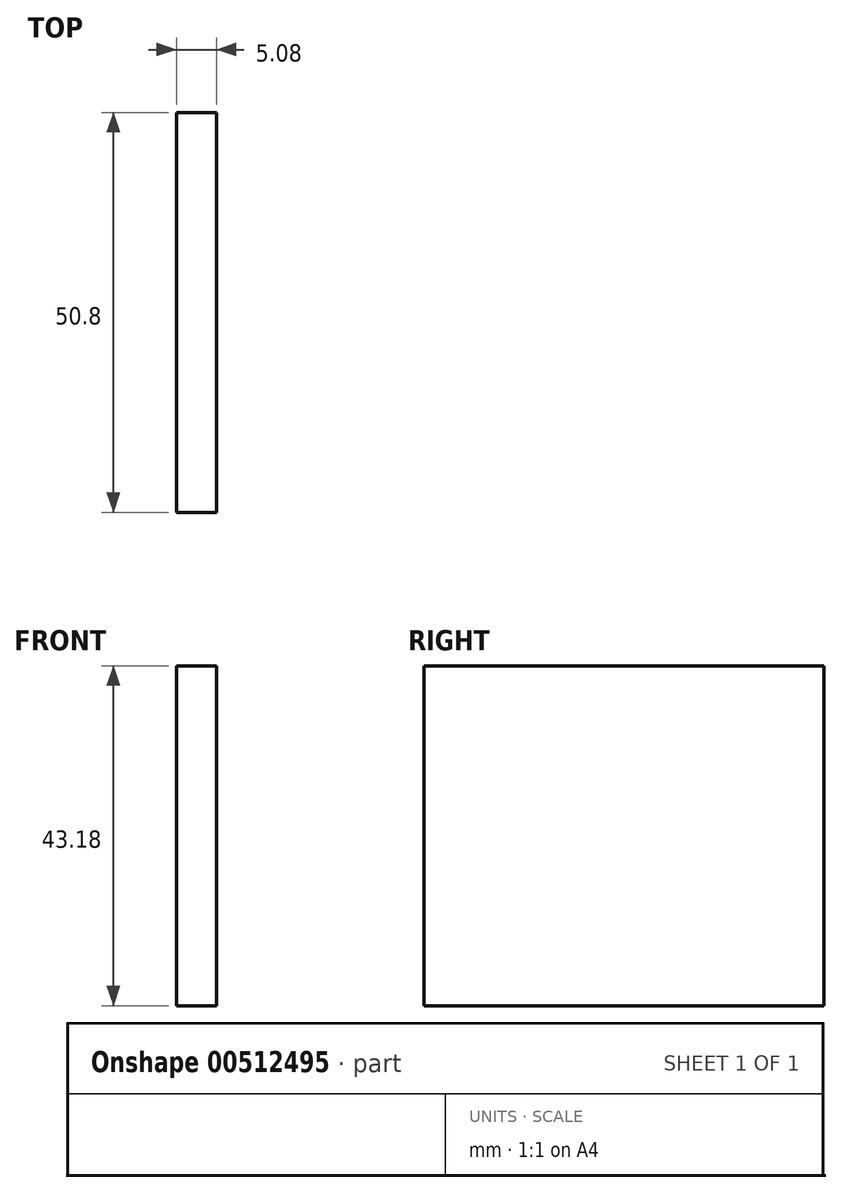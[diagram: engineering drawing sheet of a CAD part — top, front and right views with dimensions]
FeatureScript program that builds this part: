
annotation { "Feature Type Name" : "Feature", "Feature Type Description" : "" }
export const myFeature = defineFeature(function(context is Context, id is Id, definition is map)
    precondition{}
    {
        {
            var Q0;
            Q0=qCreatedBy(makeId("Right.planeOp"),FACE);
            var sketch = newSketch(context, id + "F0", { "sketchPlane" : qUnion([Q0])});
            skLineSegment(sketch, "E0.bottom", {"start": v(-14.24, 24.96) * mm, "end": v(36.56, 24.96) * mm});
            skLineSegment(sketch, "E0.top", {"start": v(-14.24, -18.22) * mm, "end": v(36.56, -18.22) * mm});
            skLineSegment(sketch, "E0.left", {"start": v(-14.24, 24.96) * mm, "end": v(-14.24, -18.22) * mm});
            skLineSegment(sketch, "E0.right", {"start": v(36.56, 24.96) * mm, "end": v(36.56, -18.22) * mm});
            skSolve(sketch);
        }
        {
            var Q0;
            Q0=makeQuery(id+"F0.imprint","IMPRINT",FACE,{"disambiguationData":[TD([[makeQuery(id+"F0.imprint","IMPRINT",EDGE,{"derivedFrom":sQuery(id+"F0.wireOp",EDGE,"E0.bottom")}),-1.0]])]});
            extrude(context, id + "F1", {"entities" : qUnion([Q0]), "depth" : 5.08 * mm});
        }
    });
